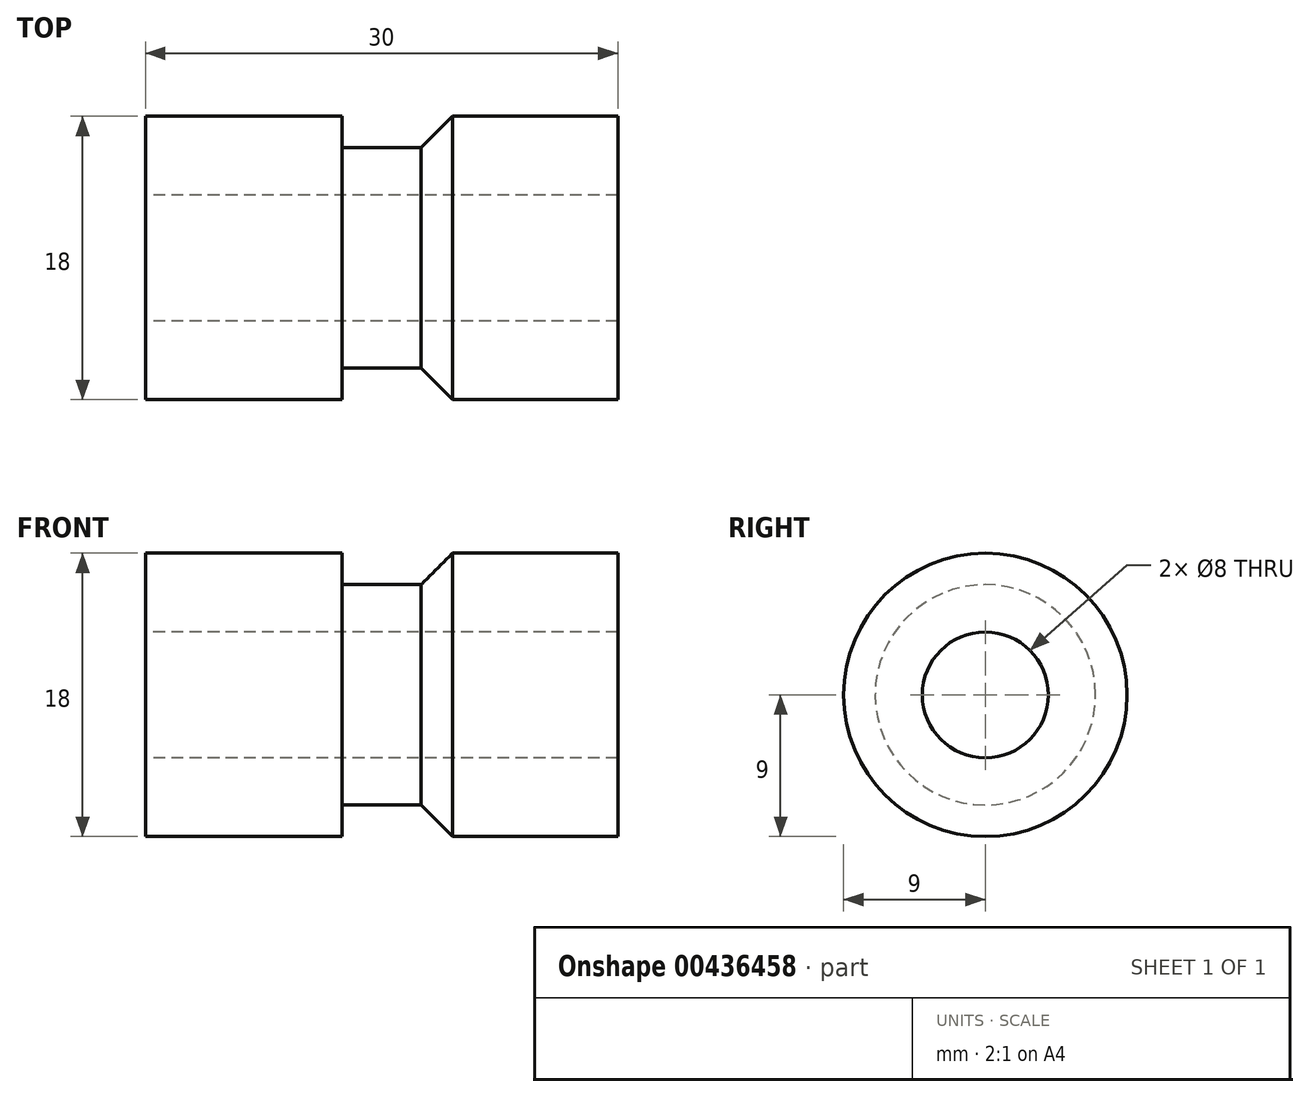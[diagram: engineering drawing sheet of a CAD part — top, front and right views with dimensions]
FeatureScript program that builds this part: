
annotation { "Feature Type Name" : "Feature", "Feature Type Description" : "" }
export const myFeature = defineFeature(function(context is Context, id is Id, definition is map)
    precondition{}
    {
        {
            var Q0;
            Q0=qCreatedBy(makeId("Front.planeOp"),FACE);
            var sketch = newSketch(context, id + "F0", { "sketchPlane" : qUnion([Q0])});
            skLineSegment(sketch, "E0", {"start": v(0, 0) * mm, "end": v(0, 4) * mm});
            skLineSegment(sketch, "E1", {"start": v(0, 4) * mm, "end": v(0, 9) * mm});
            skLineSegment(sketch, "E2", {"start": v(0, 9) * mm, "end": v(12.5, 9) * mm});
            skLineSegment(sketch, "E3", {"start": v(12.5, 9) * mm, "end": v(12.5, 7) * mm});
            skLineSegment(sketch, "E4", {"start": v(12.5, 7) * mm, "end": v(17.5, 7) * mm});
            skLineSegment(sketch, "E5", {"start": v(17.5, 7) * mm, "end": v(17.5, 9) * mm});
            skLineSegment(sketch, "E6", {"start": v(17.5, 9) * mm, "end": v(30, 9) * mm});
            skLineSegment(sketch, "E7", {"start": v(30, 9) * mm, "end": v(30, 4) * mm});
            skLineSegment(sketch, "E8", {"start": v(30, 4) * mm, "end": v(0, 4) * mm});
            skLineSegment(sketch, "E9", {"start": v(0, 0) * mm, "end": v(49.2, 0) * mm, "construction": true});
            skLineSegment(sketch, "E10", {"start": v(17.5, 7) * mm, "end": v(19.5, 9) * mm});
            skSolve(sketch);
        }
        {
            var Q0;
            Q0=makeQuery(id+"F0.imprint","IMPRINT",FACE,{"disambiguationData":[TD([[makeQuery(id+"F0.imprint","IMPRINT",EDGE,{"derivedFrom":sQuery(id+"F0.wireOp",EDGE,"E1")}),-1.0]])]});
            var Q1;
            Q1=sQuery(id+"F0.wireOp",EDGE,"E9");
            revolve(context, id + "F1", {"entities" : qUnion([Q0]), "axis" : qUnion([Q1]), "revolveType" : RevolveType.FULL});
        }
    });
